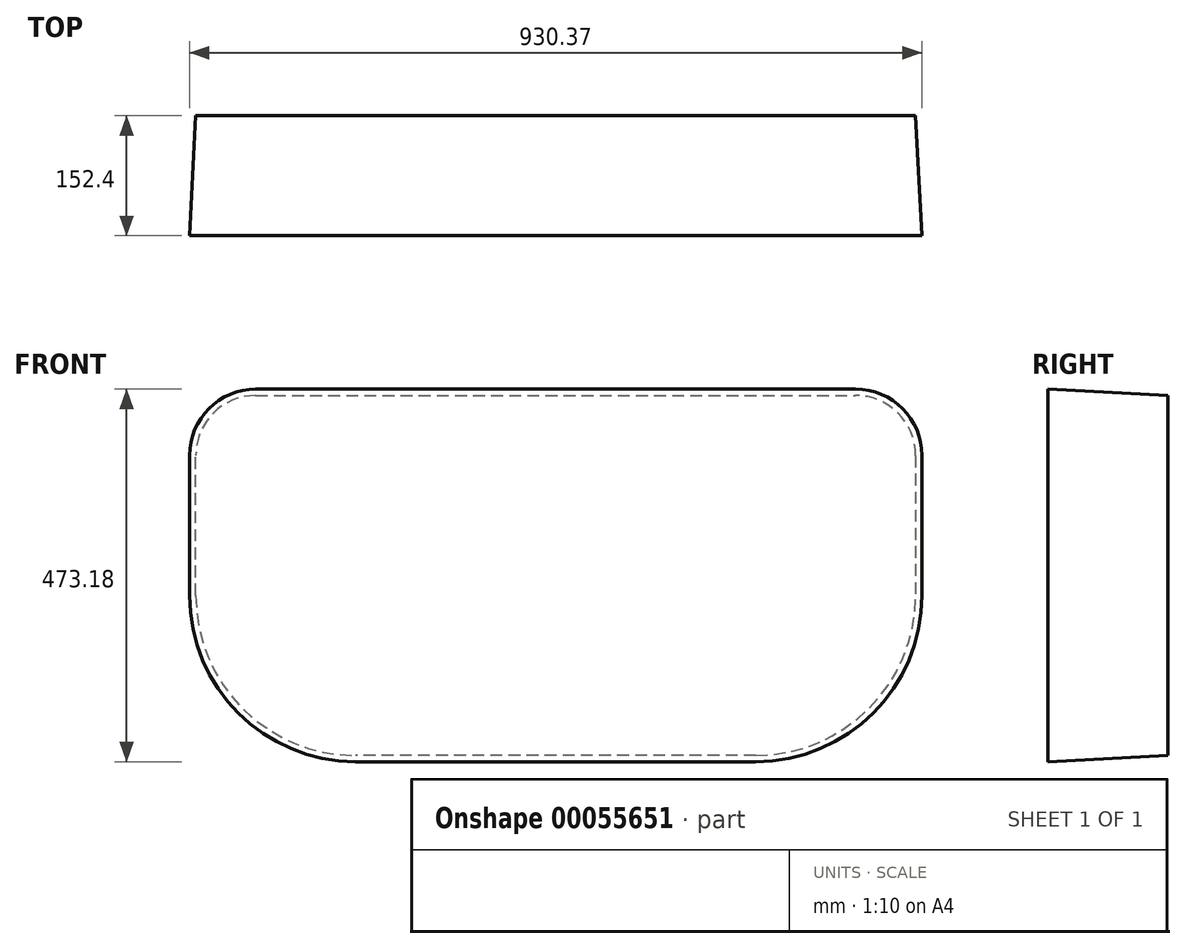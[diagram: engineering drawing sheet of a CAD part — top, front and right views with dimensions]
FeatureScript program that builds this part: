
annotation { "Feature Type Name" : "Feature", "Feature Type Description" : "" }
export const myFeature = defineFeature(function(context is Context, id is Id, definition is map)
    precondition{}
    {
        {
            var Q0;
            Q0=qCreatedBy(makeId("Front.planeOp"),FACE);
            var sketch = newSketch(context, id + "F0", { "sketchPlane" : qUnion([Q0])});
            skLineSegment(sketch, "E0.bottom", {"start": v(-377.58, 29.75) * mm, "end": v(384.42, 29.75) * mm});
            skLineSegment(sketch, "E0.top", {"start": v(-250.58, -427.45) * mm, "end": v(257.42, -427.45) * mm});
            skLineSegment(sketch, "E0.left", {"start": v(-453.78, -46.45) * mm, "end": v(-453.78, -224.25) * mm});
            skLineSegment(sketch, "E0.right", {"start": v(460.62, -46.45) * mm, "end": v(460.62, -224.25) * mm});
            skPoint(sketch, "E1.visualSharp", {"position": v(-453.78, -427.45) * mm});
            skArc(sketch, "E1.filletArc", {"start": v(-453.78, -224.25) * mm, "mid": v(-394.27, -367.93) * mm, "end": v(-250.58, -427.45) * mm});
            skPoint(sketch, "E2.visualSharp", {"position": v(460.62, -427.45) * mm});
            skArc(sketch, "E2.filletArc", {"start": v(257.42, -427.45) * mm, "mid": v(401.1, -367.93) * mm, "end": v(460.62, -224.25) * mm});
            skPoint(sketch, "E3.visualSharp", {"position": v(-453.78, 29.75) * mm});
            skArc(sketch, "E3.filletArc", {"start": v(-377.58, 29.75) * mm, "mid": v(-431.47, 7.43) * mm, "end": v(-453.78, -46.45) * mm});
            skPoint(sketch, "E4.visualSharp", {"position": v(460.62, 29.75) * mm});
            skArc(sketch, "E4.filletArc", {"start": v(460.62, -46.45) * mm, "mid": v(438.3, 7.43) * mm, "end": v(384.42, 29.75) * mm});
            skSolve(sketch);
        }
        {
            var Q0;
            Q0 = qSketchRegion(id + "F0", true);
            extrude(context, id + "F1", {"entities" : qUnion([Q0]), "depth" : 152.4 * mm, "hasDraft" : true, "draftAngle" : 3 * degree});
        }
    });
